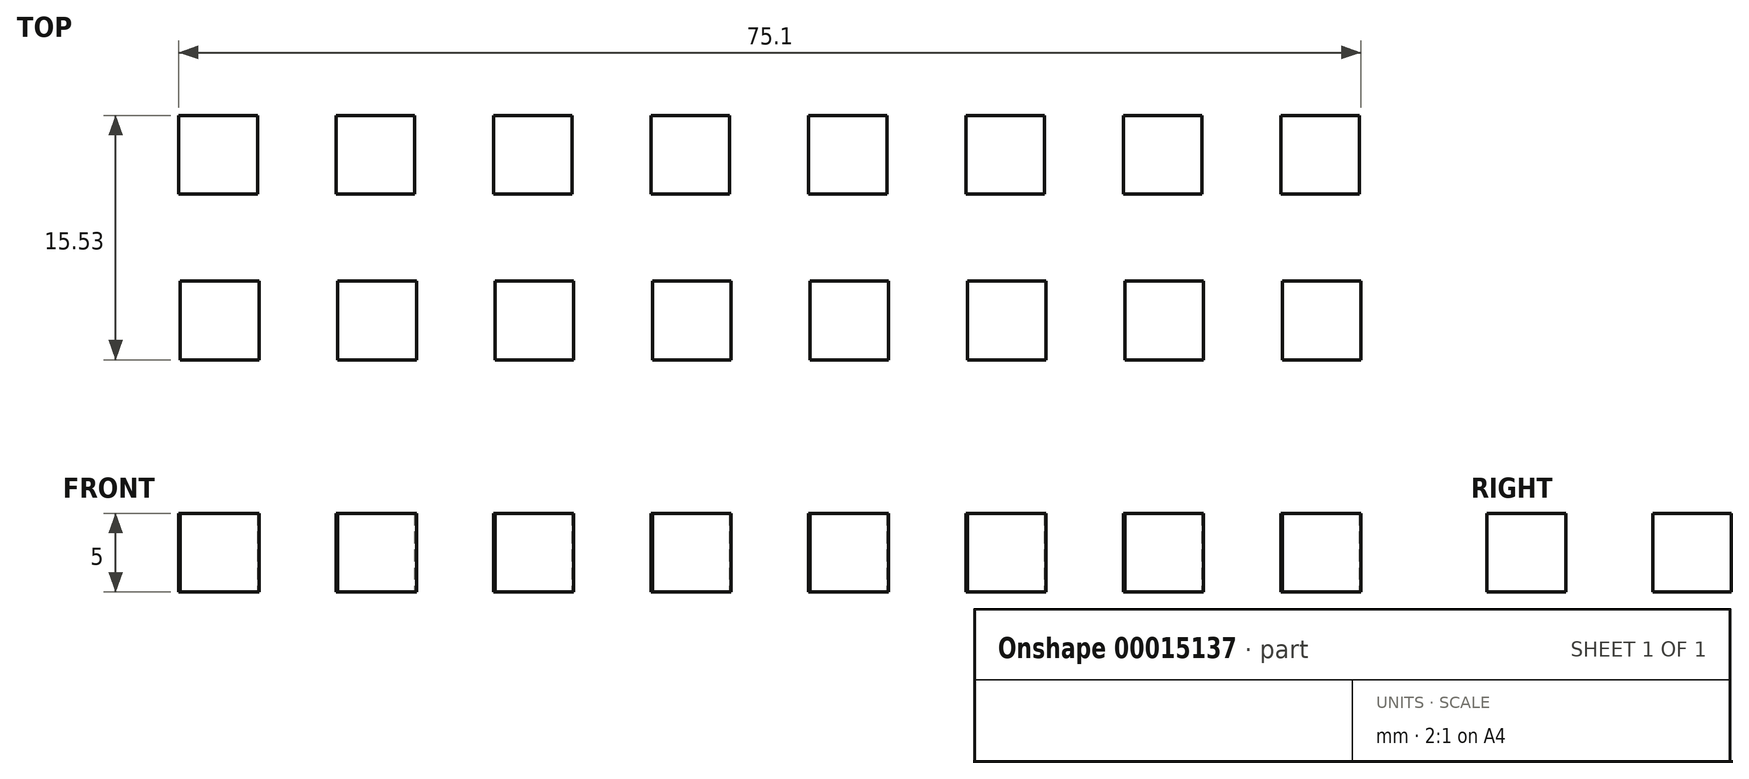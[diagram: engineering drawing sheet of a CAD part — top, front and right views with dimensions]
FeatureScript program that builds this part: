
annotation { "Feature Type Name" : "Feature", "Feature Type Description" : "" }
export const myFeature = defineFeature(function(context is Context, id is Id, definition is map)
    precondition{}
    {
        {
            var Q0;
            Q0=qCreatedBy(makeId("Top.planeOp"),FACE);
            var sketch = newSketch(context, id + "F0", { "sketchPlane" : qUnion([Q0])});
            skLineSegment(sketch, "E0.rect.bottom", {"start": v(2.5, -2.5) * mm, "end": v(-2.5, -2.5) * mm});
            skLineSegment(sketch, "E0.rect.top", {"start": v(2.5, 2.5) * mm, "end": v(-2.5, 2.5) * mm});
            skLineSegment(sketch, "E0.rect.left", {"start": v(2.5, -2.5) * mm, "end": v(2.5, 2.5) * mm});
            skLineSegment(sketch, "E0.rect.right", {"start": v(-2.5, -2.5) * mm, "end": v(-2.5, 2.5) * mm});
            skPoint(sketch, "E0.rect.middle", {"position": v(0, 0) * mm});
            skLineSegment(sketch, "E1.1.0.0", {"start": v(7.5, -2.5) * mm, "end": v(7.5, 2.5) * mm});
            skLineSegment(sketch, "E1.1.0.1", {"start": v(12.5, 2.5) * mm, "end": v(7.5, 2.5) * mm});
            skLineSegment(sketch, "E1.1.0.2", {"start": v(12.5, -2.5) * mm, "end": v(12.5, 2.5) * mm});
            skLineSegment(sketch, "E1.1.0.3", {"start": v(12.5, -2.5) * mm, "end": v(7.5, -2.5) * mm});
            skLineSegment(sketch, "E1.2.0.0", {"start": v(17.5, -2.5) * mm, "end": v(17.5, 2.5) * mm});
            skLineSegment(sketch, "E1.2.0.1", {"start": v(22.5, 2.5) * mm, "end": v(17.5, 2.5) * mm});
            skLineSegment(sketch, "E1.2.0.2", {"start": v(22.5, -2.5) * mm, "end": v(22.5, 2.5) * mm});
            skLineSegment(sketch, "E1.2.0.3", {"start": v(22.5, -2.5) * mm, "end": v(17.5, -2.5) * mm});
            skLineSegment(sketch, "E1.3.0.0", {"start": v(27.5, -2.5) * mm, "end": v(27.5, 2.5) * mm});
            skLineSegment(sketch, "E1.3.0.1", {"start": v(32.5, 2.5) * mm, "end": v(27.5, 2.5) * mm});
            skLineSegment(sketch, "E1.3.0.2", {"start": v(32.5, -2.5) * mm, "end": v(32.5, 2.5) * mm});
            skLineSegment(sketch, "E1.3.0.3", {"start": v(32.5, -2.5) * mm, "end": v(27.5, -2.5) * mm});
            skLineSegment(sketch, "E1.4.0.0", {"start": v(37.5, -2.5) * mm, "end": v(37.5, 2.5) * mm});
            skLineSegment(sketch, "E1.4.0.1", {"start": v(42.5, 2.5) * mm, "end": v(37.5, 2.5) * mm});
            skLineSegment(sketch, "E1.4.0.2", {"start": v(42.5, -2.5) * mm, "end": v(42.5, 2.5) * mm});
            skLineSegment(sketch, "E1.4.0.3", {"start": v(42.5, -2.5) * mm, "end": v(37.5, -2.5) * mm});
            skLineSegment(sketch, "E1.5.0.0", {"start": v(47.5, -2.5) * mm, "end": v(47.5, 2.5) * mm});
            skLineSegment(sketch, "E1.5.0.1", {"start": v(52.5, 2.5) * mm, "end": v(47.5, 2.5) * mm});
            skLineSegment(sketch, "E1.5.0.2", {"start": v(52.5, -2.5) * mm, "end": v(52.5, 2.5) * mm});
            skLineSegment(sketch, "E1.5.0.3", {"start": v(52.5, -2.5) * mm, "end": v(47.5, -2.5) * mm});
            skLineSegment(sketch, "E1.6.0.0", {"start": v(57.5, -2.5) * mm, "end": v(57.5, 2.5) * mm});
            skLineSegment(sketch, "E1.6.0.1", {"start": v(62.5, 2.5) * mm, "end": v(57.5, 2.5) * mm});
            skLineSegment(sketch, "E1.6.0.2", {"start": v(62.5, -2.5) * mm, "end": v(62.5, 2.5) * mm});
            skLineSegment(sketch, "E1.6.0.3", {"start": v(62.5, -2.5) * mm, "end": v(57.5, -2.5) * mm});
            skLineSegment(sketch, "E1.7.0.0", {"start": v(67.5, -2.5) * mm, "end": v(67.5, 2.5) * mm});
            skLineSegment(sketch, "E1.7.0.1", {"start": v(72.5, 2.5) * mm, "end": v(67.5, 2.5) * mm});
            skLineSegment(sketch, "E1.7.0.2", {"start": v(72.5, -2.5) * mm, "end": v(72.5, 2.5) * mm});
            skLineSegment(sketch, "E1.7.0.3", {"start": v(72.5, -2.5) * mm, "end": v(67.5, -2.5) * mm});
            skLineSegment(sketch, "E1.direction1", {"start": v(-2.5, -2.5) * mm, "end": v(7.5, -2.5) * mm, "construction": true});
            skLineSegment(sketch, "E2.rect.right", {"start": v(-2.4, -13.03) * mm, "end": v(-2.4, -8.03) * mm});
            skLineSegment(sketch, "E3.1.0.2", {"start": v(12.6, -13.03) * mm, "end": v(12.6, -8.03) * mm});
            skLineSegment(sketch, "E3.1.0.1", {"start": v(12.6, -8.03) * mm, "end": v(7.6, -8.03) * mm});
            skLineSegment(sketch, "E3.5.0.0", {"start": v(47.6, -13.03) * mm, "end": v(47.6, -8.03) * mm});
            skLineSegment(sketch, "E3.4.0.2", {"start": v(42.6, -13.03) * mm, "end": v(42.6, -8.03) * mm});
            skLineSegment(sketch, "E3.7.0.3", {"start": v(72.6, -13.03) * mm, "end": v(67.6, -13.03) * mm});
            skLineSegment(sketch, "E3.2.0.0", {"start": v(17.6, -13.03) * mm, "end": v(17.6, -8.03) * mm});
            skLineSegment(sketch, "E3.1.0.3", {"start": v(12.6, -13.03) * mm, "end": v(7.6, -13.03) * mm});
            skLineSegment(sketch, "E3.6.0.1", {"start": v(62.6, -8.03) * mm, "end": v(57.6, -8.03) * mm});
            skLineSegment(sketch, "E3.2.0.2", {"start": v(22.6, -13.03) * mm, "end": v(22.6, -8.03) * mm});
            skLineSegment(sketch, "E3.6.0.2", {"start": v(62.6, -13.03) * mm, "end": v(62.6, -8.03) * mm});
            skLineSegment(sketch, "E3.7.0.1", {"start": v(72.6, -8.03) * mm, "end": v(67.6, -8.03) * mm});
            skLineSegment(sketch, "E3.2.0.1", {"start": v(22.6, -8.03) * mm, "end": v(17.6, -8.03) * mm});
            skLineSegment(sketch, "E2.rect.top", {"start": v(2.6, -8.03) * mm, "end": v(-2.4, -8.03) * mm});
            skLineSegment(sketch, "E3.3.0.0", {"start": v(27.6, -13.03) * mm, "end": v(27.6, -8.03) * mm});
            skLineSegment(sketch, "E3.4.0.1", {"start": v(42.6, -8.03) * mm, "end": v(37.6, -8.03) * mm});
            skLineSegment(sketch, "E3.3.0.1", {"start": v(32.6, -8.03) * mm, "end": v(27.6, -8.03) * mm});
            skLineSegment(sketch, "E3.4.0.3", {"start": v(42.6, -13.03) * mm, "end": v(37.6, -13.03) * mm});
            skLineSegment(sketch, "E3.7.0.0", {"start": v(67.6, -13.03) * mm, "end": v(67.6, -8.03) * mm});
            skLineSegment(sketch, "E3.3.0.3", {"start": v(32.6, -13.03) * mm, "end": v(27.6, -13.03) * mm});
            skLineSegment(sketch, "E3.6.0.3", {"start": v(62.6, -13.03) * mm, "end": v(57.6, -13.03) * mm});
            skLineSegment(sketch, "E3.2.0.3", {"start": v(22.6, -13.03) * mm, "end": v(17.6, -13.03) * mm});
            skLineSegment(sketch, "E3.3.0.2", {"start": v(32.6, -13.03) * mm, "end": v(32.6, -8.03) * mm});
            skLineSegment(sketch, "E3.1.0.0", {"start": v(7.6, -13.03) * mm, "end": v(7.6, -8.03) * mm});
            skLineSegment(sketch, "E3.6.0.0", {"start": v(57.6, -13.03) * mm, "end": v(57.6, -8.03) * mm});
            skLineSegment(sketch, "E2.rect.left", {"start": v(2.6, -13.03) * mm, "end": v(2.6, -8.03) * mm});
            skPoint(sketch, "E2.rect.middle", {"position": v(0.1, -10.53) * mm});
            skLineSegment(sketch, "E3.4.0.0", {"start": v(37.6, -13.03) * mm, "end": v(37.6, -8.03) * mm});
            skLineSegment(sketch, "E3.5.0.1", {"start": v(52.6, -8.03) * mm, "end": v(47.6, -8.03) * mm});
            skLineSegment(sketch, "E2.rect.bottom", {"start": v(2.6, -13.03) * mm, "end": v(-2.4, -13.03) * mm});
            skLineSegment(sketch, "E3.7.0.2", {"start": v(72.6, -13.03) * mm, "end": v(72.6, -8.03) * mm});
            skLineSegment(sketch, "E3.5.0.3", {"start": v(52.6, -13.03) * mm, "end": v(47.6, -13.03) * mm});
            skLineSegment(sketch, "E3.5.0.2", {"start": v(52.6, -13.03) * mm, "end": v(52.6, -8.03) * mm});
            skLineSegment(sketch, "E3.direction1", {"start": v(-2.4, -13.03) * mm, "end": v(7.6, -13.03) * mm, "construction": true});
            skSolve(sketch);
        }
        {
            var Q0;
            Q0=makeQuery(id+"F0.imprint","IMPRINT",FACE,{"disambiguationData":[TD([[makeQuery(id+"F0.imprint","IMPRINT",EDGE,{"derivedFrom":sQuery(id+"F0.wireOp",EDGE,"E0.rect.bottom")}),-1.0]])]});
            var Q1;
            Q1=makeQuery(id+"F0.imprint","IMPRINT",FACE,{"disambiguationData":[TD([[makeQuery(id+"F0.imprint","IMPRINT",EDGE,{"derivedFrom":sQuery(id+"F0.wireOp",EDGE,"E1.1.0.0")}),-1.0]])]});
            var Q2;
            Q2=makeQuery(id+"F0.imprint","IMPRINT",FACE,{"disambiguationData":[TD([[makeQuery(id+"F0.imprint","IMPRINT",EDGE,{"derivedFrom":sQuery(id+"F0.wireOp",EDGE,"E1.2.0.0")}),-1.0]])]});
            var Q3;
            Q3=makeQuery(id+"F0.imprint","IMPRINT",FACE,{"disambiguationData":[TD([[makeQuery(id+"F0.imprint","IMPRINT",EDGE,{"derivedFrom":sQuery(id+"F0.wireOp",EDGE,"E1.3.0.0")}),-1.0]])]});
            var Q4;
            Q4=makeQuery(id+"F0.imprint","IMPRINT",FACE,{"disambiguationData":[TD([[makeQuery(id+"F0.imprint","IMPRINT",EDGE,{"derivedFrom":sQuery(id+"F0.wireOp",EDGE,"E1.4.0.0")}),-1.0]])]});
            var Q5;
            Q5=makeQuery(id+"F0.imprint","IMPRINT",FACE,{"disambiguationData":[TD([[makeQuery(id+"F0.imprint","IMPRINT",EDGE,{"derivedFrom":sQuery(id+"F0.wireOp",EDGE,"E1.5.0.0")}),-1.0]])]});
            var Q6;
            Q6=makeQuery(id+"F0.imprint","IMPRINT",FACE,{"disambiguationData":[TD([[makeQuery(id+"F0.imprint","IMPRINT",EDGE,{"derivedFrom":sQuery(id+"F0.wireOp",EDGE,"E1.6.0.0")}),-1.0]])]});
            var Q7;
            Q7=makeQuery(id+"F0.imprint","IMPRINT",FACE,{"disambiguationData":[TD([[makeQuery(id+"F0.imprint","IMPRINT",EDGE,{"derivedFrom":sQuery(id+"F0.wireOp",EDGE,"E1.7.0.0")}),-1.0]])]});
            var Q8;
            Q8=makeQuery(id+"F0.imprint","IMPRINT",FACE,{"disambiguationData":[TD([[makeQuery(id+"F0.imprint","IMPRINT",EDGE,{"derivedFrom":sQuery(id+"F0.wireOp",EDGE,"E1.8.0.0")}),-1.0]])]});
            var Q9;
            Q9=makeQuery(id+"F0.imprint","IMPRINT",FACE,{"disambiguationData":[TD([[makeQuery(id+"F0.imprint","IMPRINT",EDGE,{"derivedFrom":sQuery(id+"F0.wireOp",EDGE,"E1.9.0.0")}),-1.0]])]});
            var Q10;
            Q10=makeQuery(id+"F0.imprint","IMPRINT",FACE,{"disambiguationData":[TD([[makeQuery(id+"F0.imprint","IMPRINT",EDGE,{"derivedFrom":sQuery(id+"F0.wireOp",EDGE,"E2.rect.right")}),-1.0]])]});
            var Q11;
            Q11=makeQuery(id+"F0.imprint","IMPRINT",FACE,{"disambiguationData":[TD([[makeQuery(id+"F0.imprint","IMPRINT",EDGE,{"derivedFrom":sQuery(id+"F0.wireOp",EDGE,"E3.1.0.2")}),1.0]])]});
            var Q12;
            Q12=makeQuery(id+"F0.imprint","IMPRINT",FACE,{"disambiguationData":[TD([[makeQuery(id+"F0.imprint","IMPRINT",EDGE,{"derivedFrom":sQuery(id+"F0.wireOp",EDGE,"E3.2.0.0")}),-1.0]])]});
            var Q13;
            Q13=makeQuery(id+"F0.imprint","IMPRINT",FACE,{"disambiguationData":[TD([[makeQuery(id+"F0.imprint","IMPRINT",EDGE,{"derivedFrom":sQuery(id+"F0.wireOp",EDGE,"E3.3.0.0")}),-1.0]])]});
            var Q14;
            Q14=makeQuery(id+"F0.imprint","IMPRINT",FACE,{"disambiguationData":[TD([[makeQuery(id+"F0.imprint","IMPRINT",EDGE,{"derivedFrom":sQuery(id+"F0.wireOp",EDGE,"E3.4.0.2")}),1.0]])]});
            var Q15;
            Q15=makeQuery(id+"F0.imprint","IMPRINT",FACE,{"disambiguationData":[TD([[makeQuery(id+"F0.imprint","IMPRINT",EDGE,{"derivedFrom":sQuery(id+"F0.wireOp",EDGE,"E3.5.0.0")}),-1.0]])]});
            var Q16;
            Q16=makeQuery(id+"F0.imprint","IMPRINT",FACE,{"disambiguationData":[TD([[makeQuery(id+"F0.imprint","IMPRINT",EDGE,{"derivedFrom":sQuery(id+"F0.wireOp",EDGE,"E3.6.0.1")}),1.0]])]});
            var Q17;
            Q17=makeQuery(id+"F0.imprint","IMPRINT",FACE,{"disambiguationData":[TD([[makeQuery(id+"F0.imprint","IMPRINT",EDGE,{"derivedFrom":sQuery(id+"F0.wireOp",EDGE,"E3.7.0.3")}),-1.0]])]});
            extrude(context, id + "F1", {"entities" : qUnion([Q0, Q1, Q2, Q3, Q4, Q5, Q6, Q7, Q8, Q9, Q10, Q11, Q12, Q13, Q14, Q15, Q16, Q17]), "depth" : 5 * mm});
        }
    });
